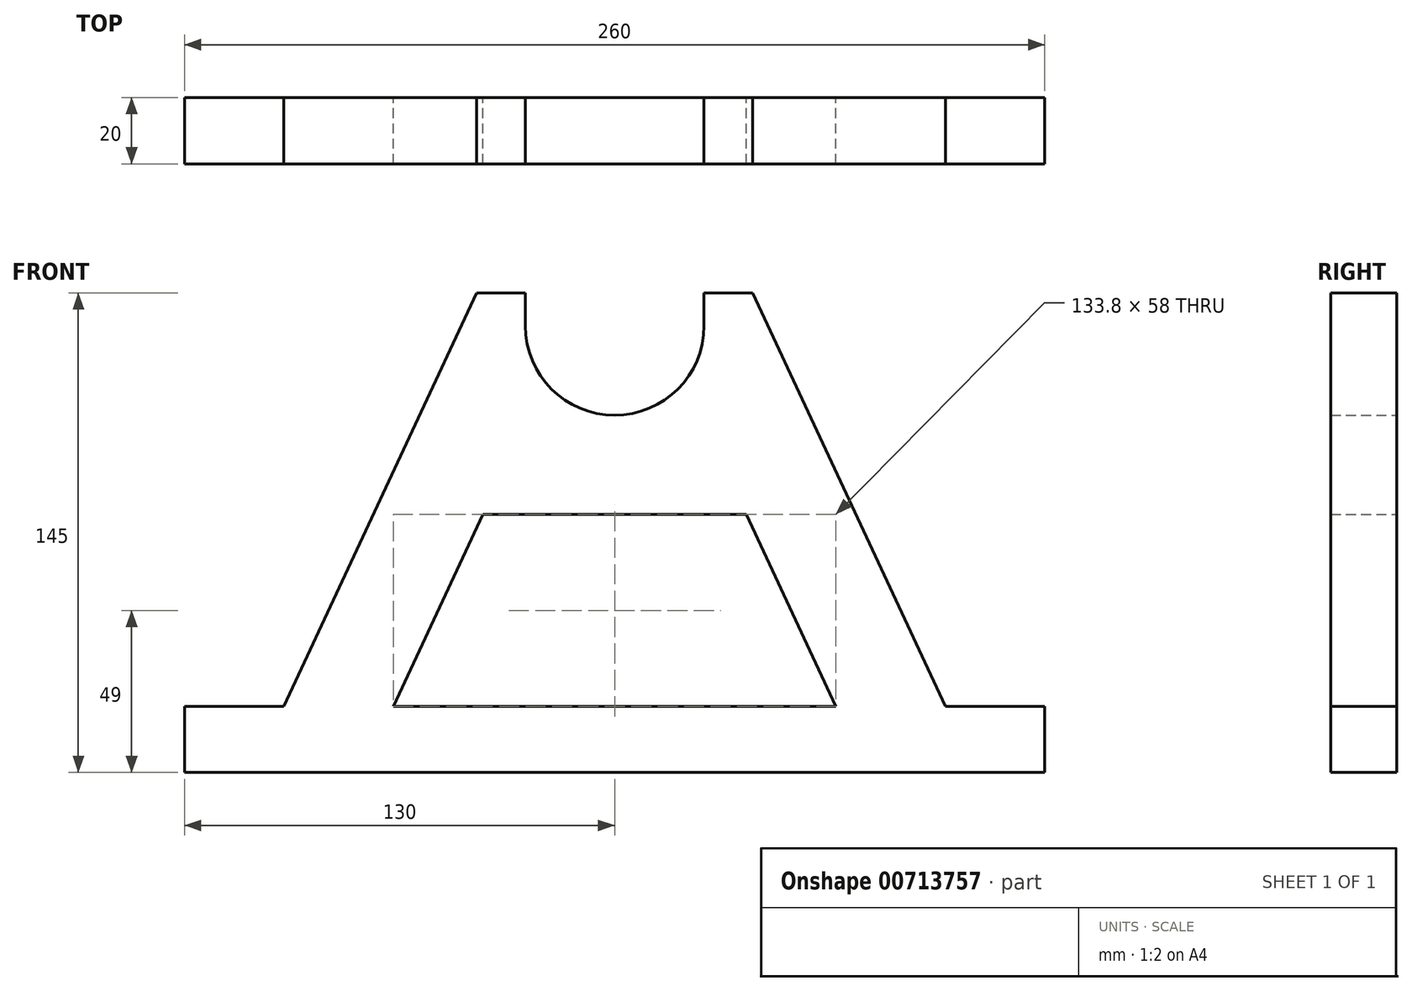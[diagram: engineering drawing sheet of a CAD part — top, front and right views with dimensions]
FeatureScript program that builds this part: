
annotation { "Feature Type Name" : "Feature", "Feature Type Description" : "" }
export const myFeature = defineFeature(function(context is Context, id is Id, definition is map)
    precondition{}
    {
        {
            var Q0;
            Q0=qCreatedBy(makeId("Front.planeOp"),FACE);
            var sketch = newSketch(context, id + "F0", { "sketchPlane" : qUnion([Q0])});
            skCircle(sketch, "E0", {"center": v(0, 135) * mm, "radius": 100 * mm});
            skLineSegment(sketch, "E1", {"start": v(-23.68, 35) * mm, "end": v(19.32, 35) * mm});
            skCircle(sketch, "E2", {"center": v(0, 135) * mm, "radius": 27 * mm});
            skSolve(sketch);
        }
        {
            var Q0;
            Q0=qCreatedBy(makeId("Front.planeOp"),FACE);
            var sketch = newSketch(context, id + "F1", { "sketchPlane" : qUnion([Q0])});
            skLineSegment(sketch, "E3", {"start": v(-130, 0) * mm, "end": v(130, 0) * mm});
            skLineSegment(sketch, "E4", {"start": v(130, 0) * mm, "end": v(130, 20) * mm});
            skLineSegment(sketch, "E5", {"start": v(130, 20) * mm, "end": v(100, 20) * mm});
            skLineSegment(sketch, "E6", {"start": v(100, 20) * mm, "end": v(41.71, 145) * mm});
            skLineSegment(sketch, "E7", {"start": v(41.71, 145) * mm, "end": v(27, 145) * mm});
            skLineSegment(sketch, "E8", {"start": v(-27, 145) * mm, "end": v(-41.71, 145) * mm});
            skLineSegment(sketch, "E9", {"start": v(-41.71, 145) * mm, "end": v(-100, 20) * mm});
            skLineSegment(sketch, "E10", {"start": v(-100, 20) * mm, "end": v(-130, 20) * mm});
            skLineSegment(sketch, "E11", {"start": v(-130, 20) * mm, "end": v(-130, 0) * mm});
            skLineSegment(sketch, "E12", {"start": v(-27, 145) * mm, "end": v(-27, 135) * mm});
            skLineSegment(sketch, "E13", {"start": v(27, 145) * mm, "end": v(27, 135) * mm});
            skArc(sketch, "E14", {"start": v(-27, 135) * mm, "mid": v(0, 108) * mm, "end": v(27, 135) * mm});
            skLineSegment(sketch, "E15", {"start": v(-66.9, 20) * mm, "end": v(-39.85, 78) * mm});
            skLineSegment(sketch, "E16", {"start": v(-39.85, 78) * mm, "end": v(39.85, 78) * mm});
            skLineSegment(sketch, "E17", {"start": v(39.85, 78) * mm, "end": v(66.9, 20) * mm});
            skLineSegment(sketch, "E18", {"start": v(-66.9, 20) * mm, "end": v(66.9, 20) * mm});
            skSolve(sketch);
        }
        {
            var Q0;
            Q0 = qSketchRegion(id + "F1", true);
            extrude(context, id + "F2", {"entities" : qUnion([Q0]), "depth" : 20 * mm, "offsetDistance" : 25 * mm});
        }
    });
